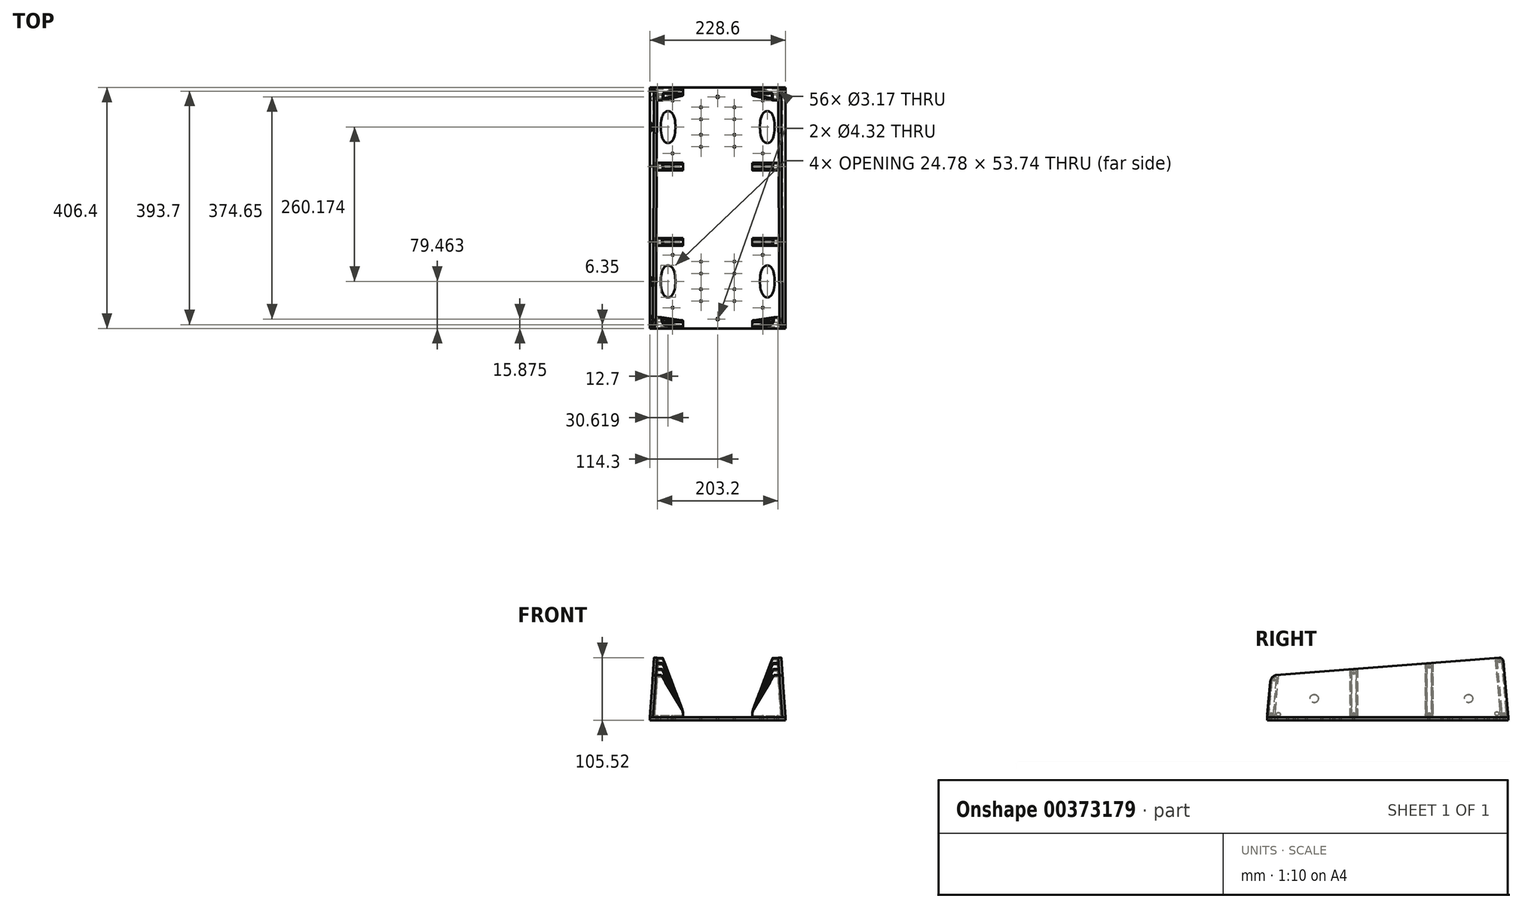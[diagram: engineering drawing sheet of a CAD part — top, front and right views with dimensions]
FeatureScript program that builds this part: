
annotation { "Feature Type Name" : "Feature", "Feature Type Description" : "" }
export const myFeature = defineFeature(function(context is Context, id is Id, definition is map)
    precondition{}
    {
        {
            var Q0;
            Q0=qCreatedBy(makeId("Top.planeOp"),FACE);
            var sketch = newSketch(context, id + "F0", { "sketchPlane" : qUnion([Q0])});
            skLineSegment(sketch, "E0.bottom", {"start": v(-114.3, 203.2) * mm, "end": v(114.3, 203.2) * mm});
            skLineSegment(sketch, "E0.top", {"start": v(-114.3, -203.2) * mm, "end": v(114.3, -203.2) * mm});
            skLineSegment(sketch, "E0.left", {"start": v(-114.3, 203.2) * mm, "end": v(-114.3, -203.2) * mm});
            skLineSegment(sketch, "E0.right", {"start": v(114.3, 203.2) * mm, "end": v(114.3, -203.2) * mm});
            skPoint(sketch, "E0.middle", {"position": v(0, 0) * mm});
            skSolve(sketch);
        }
        {
            var Q0;
            Q0=makeQuery(id+"F0.imprint","IMPRINT",FACE,{"disambiguationData":[TD([[makeQuery(id+"F0.imprint","IMPRINT",EDGE,{"derivedFrom":sQuery(id+"F0.wireOp",EDGE,"E0.bottom")}),-1.0]])]});
            extrude(context, id + "F1", {"entities" : qUnion([Q0]), "depth" : 5.08 * mm});
        }
        {
            var Q0;
            Q0=makeQuery(id+"F1.opExtrude","SWEPT_FACE",FACE,{"disambiguationData":[OSD([sQuery(id+"F0.wireOp",EDGE,"E0.bottom")])]});
            var sketch = newSketch(context, id + "F2", { "sketchPlane" : qUnion([Q0])});
            skLineSegment(sketch, "E1", {"start": v(114.3, 5.08) * mm, "end": v(107.2, 106.68) * mm});
            skLineSegment(sketch, "E2", {"start": v(107.2, 106.68) * mm, "end": v(102.13, 106.33) * mm});
            skLineSegment(sketch, "E3", {"start": v(102.13, 106.33) * mm, "end": v(109.2, 5.08) * mm});
            skLineSegment(sketch, "E4", {"start": v(109.2, 5.08) * mm, "end": v(114.3, 5.08) * mm});
            skSolve(sketch);
        }
        {
            var Q0;
            Q0=makeQuery(id+"F1.opExtrude","SWEPT_FACE",FACE,{"disambiguationData":[OSD([sQuery(id+"F0.wireOp",EDGE,"E0.top")])]});
            var sketch = newSketch(context, id + "F3", { "sketchPlane" : qUnion([Q0])});
            skLineSegment(sketch, "E5", {"start": v(-114.3, 5.08) * mm, "end": v(-109.42, 74.93) * mm});
            skLineSegment(sketch, "E6", {"start": v(-109.42, 74.93) * mm, "end": v(-104.35, 74.58) * mm});
            skLineSegment(sketch, "E7", {"start": v(-104.35, 74.58) * mm, "end": v(-109.2, 5.08) * mm});
            skLineSegment(sketch, "E8", {"start": v(-109.2, 5.08) * mm, "end": v(-114.3, 5.08) * mm});
            skSolve(sketch);
        }
        {
            var Q1;
            Q1=makeQuery(id+"F2.imprint","IMPRINT",FACE,{"disambiguationData":[TD([[makeQuery(id+"F2.imprint","IMPRINT",EDGE,{"derivedFrom":sQuery(id+"F2.wireOp",EDGE,"E1")}),1.0]])]});
            var Q2;
            Q2=makeQuery(id+"F3.imprint","IMPRINT",FACE,{"disambiguationData":[TD([[makeQuery(id+"F3.imprint","IMPRINT",EDGE,{"derivedFrom":sQuery(id+"F3.wireOp",EDGE,"E5")}),-1.0]])]});
            loft(context, id + "F4", {"sheetProfilesArray" : [{ "sheetProfileEntities" : qUnion([Q1]) }, { "sheetProfileEntities" : qUnion([Q2]) }]});
        }
        {
            var Q0;
            Q0=qCreatedBy(makeId("Right.planeOp"),FACE);
            var sketch = newSketch(context, id + "F5", { "sketchPlane" : qUnion([Q0])});
            skLineSegment(sketch, "E9", {"start": v(203.2, 5.08) * mm, "end": v(194.92, 99.72) * mm});
            skLineSegment(sketch, "E10", {"start": v(188.36, 122.29) * mm, "end": v(203.2, 122.29) * mm});
            skLineSegment(sketch, "E11", {"start": v(203.2, 122.29) * mm, "end": v(203.2, 5.08) * mm});
            skLineSegment(sketch, "E12", {"start": v(-203.2, 5.08) * mm, "end": v(-203.2, 91.13) * mm});
            skLineSegment(sketch, "E13", {"start": v(-203.2, 91.13) * mm, "end": v(-192.6, 91.13) * mm});
            skLineSegment(sketch, "E14", {"start": v(-197.97, 64.85) * mm, "end": v(-203.2, 5.08) * mm});
            skArc(sketch, "E15.filletArc", {"start": v(-188.23, 76.1) * mm, "mid": v(-194.92, 72.05) * mm, "end": v(-197.97, 64.85) * mm});
            skLineSegment(sketch, "E16", {"start": v(-192.6, 91.13) * mm, "end": v(-188.23, 76.1) * mm});
            skLineSegment(sketch, "E17", {"start": v(188.1, 105.5) * mm, "end": v(188.1, 105.5) * mm});
            skArc(sketch, "E18.filletArc", {"start": v(194.92, 99.72) * mm, "mid": v(192.7, 104.01) * mm, "end": v(188.1, 105.5) * mm});
            skLineSegment(sketch, "E19", {"start": v(188.1, 105.5) * mm, "end": v(188.36, 122.29) * mm});
            skSolve(sketch);
        }
        {
            var Q0;
            Q0=makeQuery(id+"F5.imprint","IMPRINT",FACE,{"disambiguationData":[TD([[makeQuery(id+"F5.imprint","IMPRINT",EDGE,{"derivedFrom":sQuery(id+"F5.wireOp",EDGE,"E9")}),-1.0]])]});
            var Q1;
            Q1=makeQuery(id+"F5.imprint","IMPRINT",FACE,{"disambiguationData":[TD([[makeQuery(id+"F5.imprint","IMPRINT",EDGE,{"derivedFrom":sQuery(id+"F5.wireOp",EDGE,"E12")}),-1.0]])]});
            extrude(context, id + "F6", {"entities" : qUnion([Q0, Q1]), "operationType" : NewBodyOperationType.REMOVE, "oppositeDirection" : true, "depth" : 203.2 * mm, "hasSecondDirection" : true, "secondDirectionOppositeDirection" : false, "secondDirectionDepth" : 147.32 * mm});
        }
        {
            var Q0;
            Q0=qCreatedBy(makeId("Front.planeOp"),FACE);
            cPlane(context, id + "F7", {"entities" : qUnion([Q0]), "cplaneType" : CPlaneType.OFFSET, "offset" : 127 * mm, "width" : 152.4 * mm, "height" : 152.4 * mm});
        }
        {
            var Q0;
            Q0=makeQuery(id+"F1.opExtrude","CAP_FACE",FACE,{"disambiguationData":[OSD([sQuery(id+"F0.wireOp",EDGE,"E0.bottom"),sQuery(id+"F0.wireOp",EDGE,"E0.top"),sQuery(id+"F0.wireOp",EDGE,"E0.left"),sQuery(id+"F0.wireOp",EDGE,"E0.right")])],"isStart":false});
            var sketch = newSketch(context, id + "F8", { "sketchPlane" : qUnion([Q0])});
            skCircle(sketch, "E20.0", {"center": v(-75.97, -168.27) * mm, "radius": 1.59 * mm});
            skCircle(sketch, "E21.0", {"center": v(-28.17, -157.07) * mm, "radius": 1.59 * mm});
            skCircle(sketch, "E22.0", {"center": v(-28.17, -136.9) * mm, "radius": 1.59 * mm});
            skCircle(sketch, "E23.0", {"center": v(-28.17, -110.58) * mm, "radius": 1.59 * mm});
            skCircle(sketch, "E24.0", {"center": v(-28.17, -90.4) * mm, "radius": 1.59 * mm});
            skCircle(sketch, "E25.0", {"center": v(-75.97, -79.2) * mm, "radius": 1.59 * mm});
            skFitSpline(sketch, "E26.0", {"points": [v(-83.68, -96.87) * mm, v(-83.23, -96.87) * mm, v(-82.57, -96.93) * mm, v(-81.73, -97.12) * mm, v(-80.9, -97.37) * mm, v(-79.92, -97.8) * mm, v(-78.87, -98.46) * mm, v(-77.94, -99.21) * mm, v(-77.13, -100.03) * mm, v(-76.43, -100.88) * mm, v(-75.8, -101.77) * mm, v(-75.26, -102.67) * mm, v(-74.78, -103.59) * mm, v(-74.35, -104.5) * mm, v(-73.85, -105.73) * mm, v(-73.32, -107.27) * mm, v(-72.81, -109.13) * mm, v(-72.4, -110.98) * mm, v(-71.98, -113.43) * mm, v(-71.6, -116.47) * mm, v(-71.37, -120.1) * mm, v(-71.29, -123.74) * mm, v(-71.37, -127.4) * mm, v(-71.61, -131.06) * mm, v(-71.99, -134.1) * mm, v(-72.42, -136.56) * mm, v(-72.83, -138.41) * mm, v(-73.34, -140.26) * mm, v(-73.87, -141.8) * mm, v(-74.38, -143.03) * mm, v(-74.8, -143.95) * mm, v(-75.29, -144.85) * mm, v(-75.83, -145.74) * mm, v(-76.44, -146.61) * mm, v(-77.15, -147.47) * mm, v(-77.96, -148.28) * mm, v(-78.88, -149.02) * mm, v(-79.75, -149.56) * mm, v(-80.5, -149.93) * mm, v(-81.1, -150.16) * mm, v(-81.72, -150.35) * mm, v(-82.57, -150.54) * mm, v(-83.24, -150.6) * mm, v(-83.68, -150.6) * mm]});
            skFitSpline(sketch, "E26.1", {"points": [v(-83.68, -96.87) * mm, v(-84.13, -96.87) * mm, v(-84.79, -96.93) * mm, v(-85.64, -97.12) * mm, v(-86.47, -97.37) * mm, v(-87.45, -97.8) * mm, v(-88.5, -98.46) * mm, v(-89.42, -99.21) * mm, v(-90.23, -100.03) * mm, v(-90.94, -100.88) * mm, v(-91.56, -101.77) * mm, v(-92.1, -102.67) * mm, v(-92.59, -103.59) * mm, v(-93, -104.5) * mm, v(-93.51, -105.73) * mm, v(-94.04, -107.27) * mm, v(-94.55, -109.13) * mm, v(-94.96, -110.98) * mm, v(-95.38, -113.43) * mm, v(-95.75, -116.47) * mm, v(-96, -120.1) * mm, v(-96.07, -123.74) * mm, v(-96, -127.4) * mm, v(-95.75, -131.06) * mm, v(-95.38, -134.1) * mm, v(-94.94, -136.56) * mm, v(-94.53, -138.41) * mm, v(-94.02, -140.26) * mm, v(-93.5, -141.8) * mm, v(-92.99, -143.03) * mm, v(-92.56, -143.95) * mm, v(-92.08, -144.85) * mm, v(-91.53, -145.74) * mm, v(-90.92, -146.61) * mm, v(-90.21, -147.47) * mm, v(-89.4, -148.28) * mm, v(-88.48, -149.02) * mm, v(-87.61, -149.56) * mm, v(-86.85, -149.93) * mm, v(-86.26, -150.16) * mm, v(-85.65, -150.35) * mm, v(-84.79, -150.54) * mm, v(-84.13, -150.6) * mm, v(-83.68, -150.6) * mm]});
            skLineSegment(sketch, "E27", {"start": v(-67.72, -127) * mm, "end": v(-28.17, -127) * mm, "construction": true});
            skLineSegment(sketch, "E28", {"start": v(-88.7, 6.35) * mm, "end": v(82.7, 6.35) * mm, "construction": true});
            skLineSegment(sketch, "E29", {"start": v(0, 92.42) * mm, "end": v(0, -98.09) * mm, "construction": true});
            skCircle(sketch, "E30.MirrorC", {"center": v(28.17, -136.9) * mm, "radius": 1.59 * mm});
            skCircle(sketch, "E31.MirrorC", {"center": v(28.17, -110.58) * mm, "radius": 1.59 * mm});
            skCircle(sketch, "E32.MirrorC", {"center": v(28.17, -157.07) * mm, "radius": 1.59 * mm});
            skCircle(sketch, "E33.MirrorC", {"center": v(75.97, -79.2) * mm, "radius": 1.59 * mm});
            skLineSegment(sketch, "E34.MirrorCS", {"start": v(67.72, -127) * mm, "end": v(28.17, -127) * mm, "construction": true});
            skCircle(sketch, "E35.MirrorC", {"center": v(28.17, -90.4) * mm, "radius": 1.59 * mm});
            skCircle(sketch, "E36.MirrorC", {"center": v(75.97, -168.27) * mm, "radius": 1.59 * mm});
            skFitSpline(sketch, "E37.MirrorCS", {"points": [v(83.68, -96.87) * mm, v(84.13, -96.87) * mm, v(84.79, -96.93) * mm, v(85.64, -97.12) * mm, v(86.47, -97.37) * mm, v(87.45, -97.8) * mm, v(88.5, -98.46) * mm, v(89.42, -99.21) * mm, v(90.23, -100.03) * mm, v(90.94, -100.88) * mm, v(91.56, -101.77) * mm, v(92.1, -102.67) * mm, v(92.59, -103.59) * mm, v(93, -104.5) * mm, v(93.51, -105.73) * mm, v(94.04, -107.27) * mm, v(94.55, -109.13) * mm, v(94.96, -110.98) * mm, v(95.38, -113.43) * mm, v(95.75, -116.47) * mm, v(96, -120.1) * mm, v(96.07, -123.74) * mm, v(96, -127.4) * mm, v(95.75, -131.06) * mm, v(95.38, -134.1) * mm, v(94.94, -136.56) * mm, v(94.53, -138.41) * mm, v(94.02, -140.26) * mm, v(93.5, -141.8) * mm, v(92.99, -143.03) * mm, v(92.56, -143.95) * mm, v(92.08, -144.85) * mm, v(91.53, -145.74) * mm, v(90.92, -146.61) * mm, v(90.21, -147.47) * mm, v(89.4, -148.28) * mm, v(88.48, -149.02) * mm, v(87.61, -149.56) * mm, v(86.85, -149.93) * mm, v(86.26, -150.16) * mm, v(85.65, -150.35) * mm, v(84.79, -150.54) * mm, v(84.13, -150.6) * mm, v(83.68, -150.6) * mm]});
            skFitSpline(sketch, "E38.MirrorCS", {"points": [v(83.68, -96.87) * mm, v(83.23, -96.87) * mm, v(82.57, -96.93) * mm, v(81.73, -97.12) * mm, v(80.9, -97.37) * mm, v(79.92, -97.8) * mm, v(78.87, -98.46) * mm, v(77.94, -99.21) * mm, v(77.13, -100.03) * mm, v(76.43, -100.88) * mm, v(75.8, -101.77) * mm, v(75.26, -102.67) * mm, v(74.78, -103.59) * mm, v(74.35, -104.5) * mm, v(73.85, -105.73) * mm, v(73.32, -107.27) * mm, v(72.81, -109.13) * mm, v(72.4, -110.98) * mm, v(71.98, -113.43) * mm, v(71.6, -116.47) * mm, v(71.37, -120.1) * mm, v(71.29, -123.74) * mm, v(71.37, -127.4) * mm, v(71.61, -131.06) * mm, v(71.99, -134.1) * mm, v(72.42, -136.56) * mm, v(72.83, -138.41) * mm, v(73.34, -140.26) * mm, v(73.87, -141.8) * mm, v(74.38, -143.03) * mm, v(74.8, -143.95) * mm, v(75.29, -144.85) * mm, v(75.83, -145.74) * mm, v(76.44, -146.61) * mm, v(77.15, -147.47) * mm, v(77.96, -148.28) * mm, v(78.88, -149.02) * mm, v(79.75, -149.56) * mm, v(80.5, -149.93) * mm, v(81.1, -150.16) * mm, v(81.72, -150.35) * mm, v(82.57, -150.54) * mm, v(83.24, -150.6) * mm, v(83.68, -150.6) * mm]});
            skCircle(sketch, "E39.MirrorC", {"center": v(28.17, 169.77) * mm, "radius": 1.59 * mm});
            skCircle(sketch, "E40.MirrorC", {"center": v(75.97, 91.9) * mm, "radius": 1.59 * mm});
            skCircle(sketch, "E41.MirrorC", {"center": v(28.17, 149.6) * mm, "radius": 1.59 * mm});
            skCircle(sketch, "E42.MirrorC", {"center": v(28.17, 123.28) * mm, "radius": 1.59 * mm});
            skCircle(sketch, "E43.MirrorC", {"center": v(75.97, 180.97) * mm, "radius": 1.59 * mm});
            skCircle(sketch, "E44.MirrorC", {"center": v(28.17, 103.1) * mm, "radius": 1.59 * mm});
            skLineSegment(sketch, "E45.MirrorCS", {"start": v(67.72, 139.7) * mm, "end": v(28.17, 139.7) * mm, "construction": true});
            skFitSpline(sketch, "E46.MirrorCS", {"points": [v(83.68, 109.57) * mm, v(84.13, 109.57) * mm, v(84.79, 109.63) * mm, v(85.64, 109.82) * mm, v(86.47, 110.07) * mm, v(87.45, 110.5) * mm, v(88.5, 111.16) * mm, v(89.42, 111.91) * mm, v(90.23, 112.73) * mm, v(90.94, 113.58) * mm, v(91.56, 114.47) * mm, v(92.1, 115.37) * mm, v(92.59, 116.29) * mm, v(93, 117.2) * mm, v(93.51, 118.43) * mm, v(94.04, 119.97) * mm, v(94.55, 121.83) * mm, v(94.96, 123.68) * mm, v(95.38, 126.13) * mm, v(95.75, 129.17) * mm, v(96, 132.8) * mm, v(96.07, 136.44) * mm, v(96, 140.1) * mm, v(95.75, 143.76) * mm, v(95.38, 146.8) * mm, v(94.94, 149.26) * mm, v(94.53, 151.11) * mm, v(94.02, 152.96) * mm, v(93.5, 154.5) * mm, v(92.99, 155.73) * mm, v(92.56, 156.65) * mm, v(92.08, 157.55) * mm, v(91.53, 158.44) * mm, v(90.92, 159.31) * mm, v(90.21, 160.17) * mm, v(89.4, 160.98) * mm, v(88.48, 161.72) * mm, v(87.61, 162.26) * mm, v(86.85, 162.63) * mm, v(86.26, 162.86) * mm, v(85.65, 163.05) * mm, v(84.79, 163.24) * mm, v(84.13, 163.3) * mm, v(83.68, 163.3) * mm]});
            skFitSpline(sketch, "E47.MirrorCS", {"points": [v(83.68, 109.57) * mm, v(83.23, 109.57) * mm, v(82.57, 109.63) * mm, v(81.73, 109.82) * mm, v(80.9, 110.07) * mm, v(79.92, 110.5) * mm, v(78.87, 111.16) * mm, v(77.94, 111.91) * mm, v(77.13, 112.73) * mm, v(76.43, 113.58) * mm, v(75.8, 114.47) * mm, v(75.26, 115.37) * mm, v(74.78, 116.29) * mm, v(74.35, 117.2) * mm, v(73.85, 118.43) * mm, v(73.32, 119.97) * mm, v(72.81, 121.83) * mm, v(72.4, 123.68) * mm, v(71.98, 126.13) * mm, v(71.6, 129.17) * mm, v(71.37, 132.8) * mm, v(71.29, 136.44) * mm, v(71.37, 140.1) * mm, v(71.61, 143.76) * mm, v(71.99, 146.8) * mm, v(72.42, 149.26) * mm, v(72.83, 151.11) * mm, v(73.34, 152.96) * mm, v(73.87, 154.5) * mm, v(74.38, 155.73) * mm, v(74.8, 156.65) * mm, v(75.29, 157.55) * mm, v(75.83, 158.44) * mm, v(76.44, 159.31) * mm, v(77.15, 160.17) * mm, v(77.96, 160.98) * mm, v(78.88, 161.72) * mm, v(79.75, 162.26) * mm, v(80.5, 162.63) * mm, v(81.1, 162.86) * mm, v(81.72, 163.05) * mm, v(82.57, 163.24) * mm, v(83.24, 163.3) * mm, v(83.68, 163.3) * mm]});
            skCircle(sketch, "E48.MirrorC", {"center": v(-28.17, 123.28) * mm, "radius": 1.59 * mm});
            skCircle(sketch, "E49.MirrorC", {"center": v(-75.97, 91.9) * mm, "radius": 1.59 * mm});
            skCircle(sketch, "E50.MirrorC", {"center": v(-28.17, 103.1) * mm, "radius": 1.59 * mm});
            skFitSpline(sketch, "E51.MirrorCS", {"points": [v(-83.68, 109.57) * mm, v(-83.23, 109.57) * mm, v(-82.57, 109.63) * mm, v(-81.73, 109.82) * mm, v(-80.9, 110.07) * mm, v(-79.92, 110.5) * mm, v(-78.87, 111.16) * mm, v(-77.94, 111.91) * mm, v(-77.13, 112.73) * mm, v(-76.43, 113.58) * mm, v(-75.8, 114.47) * mm, v(-75.26, 115.37) * mm, v(-74.78, 116.29) * mm, v(-74.35, 117.2) * mm, v(-73.85, 118.43) * mm, v(-73.32, 119.97) * mm, v(-72.81, 121.83) * mm, v(-72.4, 123.68) * mm, v(-71.98, 126.13) * mm, v(-71.6, 129.17) * mm, v(-71.37, 132.8) * mm, v(-71.29, 136.44) * mm, v(-71.37, 140.1) * mm, v(-71.61, 143.76) * mm, v(-71.99, 146.8) * mm, v(-72.42, 149.26) * mm, v(-72.83, 151.11) * mm, v(-73.34, 152.96) * mm, v(-73.87, 154.5) * mm, v(-74.38, 155.73) * mm, v(-74.8, 156.65) * mm, v(-75.29, 157.55) * mm, v(-75.83, 158.44) * mm, v(-76.44, 159.31) * mm, v(-77.15, 160.17) * mm, v(-77.96, 160.98) * mm, v(-78.88, 161.72) * mm, v(-79.75, 162.26) * mm, v(-80.5, 162.63) * mm, v(-81.1, 162.86) * mm, v(-81.72, 163.05) * mm, v(-82.57, 163.24) * mm, v(-83.24, 163.3) * mm, v(-83.68, 163.3) * mm]});
            skLineSegment(sketch, "E52.MirrorCS", {"start": v(-67.72, 139.7) * mm, "end": v(-28.17, 139.7) * mm, "construction": true});
            skCircle(sketch, "E53.MirrorC", {"center": v(-75.97, 180.97) * mm, "radius": 1.59 * mm});
            skCircle(sketch, "E54.MirrorC", {"center": v(-28.17, 169.77) * mm, "radius": 1.59 * mm});
            skCircle(sketch, "E55.MirrorC", {"center": v(-28.17, 149.6) * mm, "radius": 1.59 * mm});
            skFitSpline(sketch, "E56.MirrorCS", {"points": [v(-83.68, 109.57) * mm, v(-84.13, 109.57) * mm, v(-84.79, 109.63) * mm, v(-85.64, 109.82) * mm, v(-86.47, 110.07) * mm, v(-87.45, 110.5) * mm, v(-88.5, 111.16) * mm, v(-89.42, 111.91) * mm, v(-90.23, 112.73) * mm, v(-90.94, 113.58) * mm, v(-91.56, 114.47) * mm, v(-92.1, 115.37) * mm, v(-92.59, 116.29) * mm, v(-93, 117.2) * mm, v(-93.51, 118.43) * mm, v(-94.04, 119.97) * mm, v(-94.55, 121.83) * mm, v(-94.96, 123.68) * mm, v(-95.38, 126.13) * mm, v(-95.75, 129.17) * mm, v(-96, 132.8) * mm, v(-96.07, 136.44) * mm, v(-96, 140.1) * mm, v(-95.75, 143.76) * mm, v(-95.38, 146.8) * mm, v(-94.94, 149.26) * mm, v(-94.53, 151.11) * mm, v(-94.02, 152.96) * mm, v(-93.5, 154.5) * mm, v(-92.99, 155.73) * mm, v(-92.56, 156.65) * mm, v(-92.08, 157.55) * mm, v(-91.53, 158.44) * mm, v(-90.92, 159.31) * mm, v(-90.21, 160.17) * mm, v(-89.4, 160.98) * mm, v(-88.48, 161.72) * mm, v(-87.61, 162.26) * mm, v(-86.85, 162.63) * mm, v(-86.26, 162.86) * mm, v(-85.65, 163.05) * mm, v(-84.79, 163.24) * mm, v(-84.13, 163.3) * mm, v(-83.68, 163.3) * mm]});
            skPoint(sketch, "E57.middle", {"position": v(0, 0) * mm});
            skCircle(sketch, "E58", {"center": v(-101.6, -196.85) * mm, "radius": 1.59 * mm});
            skCircle(sketch, "E59", {"center": v(-76.2, -196.85) * mm, "radius": 1.59 * mm});
            skCircle(sketch, "E60.MirrorC", {"center": v(-76.2, -57.15) * mm, "radius": 1.59 * mm});
            skCircle(sketch, "E61.MirrorC", {"center": v(-101.6, -57.15) * mm, "radius": 1.59 * mm});
            skCircle(sketch, "E62", {"center": v(-101.6, 196.85) * mm, "radius": 1.59 * mm});
            skCircle(sketch, "E63", {"center": v(-76.2, 196.85) * mm, "radius": 1.59 * mm});
            skCircle(sketch, "E64.MirrorC", {"center": v(101.6, 196.85) * mm, "radius": 1.59 * mm});
            skCircle(sketch, "E65.MirrorC", {"center": v(76.2, 196.85) * mm, "radius": 1.59 * mm});
            skCircle(sketch, "E66.MirrorC", {"center": v(101.6, -57.15) * mm, "radius": 1.59 * mm});
            skCircle(sketch, "E67.MirrorC", {"center": v(76.2, -57.15) * mm, "radius": 1.59 * mm});
            skCircle(sketch, "E68.MirrorC", {"center": v(101.6, -196.85) * mm, "radius": 1.59 * mm});
            skCircle(sketch, "E69.MirrorC", {"center": v(76.2, -196.85) * mm, "radius": 1.59 * mm});
            skCircle(sketch, "E70", {"center": v(-101.6, 69.85) * mm, "radius": 1.59 * mm});
            skCircle(sketch, "E71", {"center": v(-76.2, 69.85) * mm, "radius": 1.59 * mm});
            skCircle(sketch, "E72.MirrorC", {"center": v(76.2, 69.85) * mm, "radius": 1.59 * mm});
            skCircle(sketch, "E73.MirrorC", {"center": v(101.6, 69.85) * mm, "radius": 1.59 * mm});
            skPoint(sketch, "E57.right.start.orphan", {"position": v(114.3, 203.2) * mm});
            skPoint(sketch, "E57.left.start.orphan", {"position": v(-114.3, 203.2) * mm});
            skPoint(sketch, "E57.top.end.orphan", {"position": v(114.3, -203.2) * mm});
            skPoint(sketch, "E57.top.start.orphan", {"position": v(-114.3, -203.2) * mm});
            skCircle(sketch, "E74", {"center": v(0, 187.33) * mm, "radius": 2.16 * mm});
            skCircle(sketch, "E75", {"center": v(0, -187.32) * mm, "radius": 2.16 * mm});
            skSolve(sketch);
        }
        {
            var Q0;
            Q0=makeQuery(id+"F4.opLoft","SWEPT_FACE",FACE,{"disambiguationData":[OSD([sQuery(id+"F0.wireOp",EDGE,"E0.bottom"),sQuery(id+"F0.wireOp",EDGE,"E0.top"),sQuery(id+"F0.wireOp",EDGE,"E0.left"),sQuery(id+"F2.wireOp",EDGE,"E1"),sQuery(id+"F2.wireOp",EDGE,"E2"),sQuery(id+"F2.wireOp",EDGE,"E4"),sQuery(id+"F3.wireOp",EDGE,"E5"),sQuery(id+"F3.wireOp",EDGE,"E6"),sQuery(id+"F3.wireOp",EDGE,"E8")])]});
            var sketch = newSketch(context, id + "F9", { "sketchPlane" : qUnion([Q0])});
            skLineSegment(sketch, "E76", {"start": v(197.97, 57) * mm, "end": v(197.97, 57) * mm});
            skLineSegment(sketch, "E77", {"start": v(196.83, -2.9) * mm, "end": v(190.63, 68.1) * mm, "construction": true});
            skLineSegment(sketch, "E78", {"start": v(-196.83, -2.9) * mm, "end": v(-188.04, 97.76) * mm, "construction": true});
            skLineSegment(sketch, "E79", {"start": v(-69.85, -2.9) * mm, "end": v(-69.85, 88.5) * mm, "construction": true});
            skLineSegment(sketch, "E80", {"start": v(57.15, -2.9) * mm, "end": v(57.15, 78.55) * mm, "construction": true});
            skCircle(sketch, "E81", {"center": v(-196.27, 3.42) * mm, "radius": 1.59 * mm});
            skCircle(sketch, "E82", {"center": v(-188.6, 91.43) * mm, "radius": 1.59 * mm});
            skCircle(sketch, "E83", {"center": v(-69.85, 82.15) * mm, "radius": 1.59 * mm});
            skCircle(sketch, "E84", {"center": v(-69.85, 3.44) * mm, "radius": 1.59 * mm});
            skCircle(sketch, "E85", {"center": v(57.15, 72.2) * mm, "radius": 1.59 * mm});
            skCircle(sketch, "E86", {"center": v(57.15, 3.44) * mm, "radius": 1.59 * mm});
            skCircle(sketch, "E87", {"center": v(196.27, 3.42) * mm, "radius": 1.59 * mm});
            skCircle(sketch, "E88", {"center": v(191.3, 60.5) * mm, "radius": 1.59 * mm});
            skCircle(sketch, "E89", {"center": v(184.15, 2.17) * mm, "radius": 3.24 * mm});
            skCircle(sketch, "E90", {"center": v(-184.15, 3.44) * mm, "radius": 3.24 * mm});
            skCircle(sketch, "E91", {"center": v(123.74, 28.84) * mm, "radius": 6.99 * mm});
            skCircle(sketch, "E92", {"center": v(-136.44, 28.84) * mm, "radius": 6.99 * mm});
            skSolve(sketch);
        }
        {
            var Q0;
            Q0=makeQuery(id+"F4.opLoft","SWEPT_BODY",BODY,{"disambiguationData":[OSD([makeQuery(id+"F2.imprint","IMPRINT",FACE,{"disambiguationData":[TD([[makeQuery(id+"F2.imprint","IMPRINT",EDGE,{"derivedFrom":sQuery(id+"F2.wireOp",EDGE,"E1")}),1.0]])]}),makeQuery(id+"F3.imprint","IMPRINT",FACE,{"disambiguationData":[TD([[makeQuery(id+"F3.imprint","IMPRINT",EDGE,{"derivedFrom":sQuery(id+"F3.wireOp",EDGE,"E5")}),-1.0]])]})])]});
            var Q1;
            Q1=qCreatedBy(makeId("Right.planeOp"),FACE);
            mirror(context, id + "F10", {"entities" : qUnion([Q0]), "mirrorPlane" : qUnion([Q1])});
        }
        {
            var Q0;
            Q0=makeQuery(id+"F6.boolean.opBoolean","COPY",FACE,{"derivedFrom":makeQuery(id+"F6.opExtrude","SWEPT_FACE",FACE,{"disambiguationData":[OSD([sQuery(id+"F5.wireOp",EDGE,"E14")])]})});
            cPlane(context, id + "F11", {"entities" : qUnion([Q0]), "cplaneType" : CPlaneType.OFFSET, "offset" : 0 * mm, "width" : 152.4 * mm, "height" : 152.4 * mm});
        }
        {
            var Q0;
            Q0=qCreatedBy(id+"F11.planeOp",FACE);
            var sketch = newSketch(context, id + "F12", { "sketchPlane" : qUnion([Q0])});
            skLineSegment(sketch, "E93", {"start": v(-58.4, -12.65) * mm, "end": v(-109.2, -12.65) * mm});
            skLineSegment(sketch, "E94", {"start": v(-109.2, -12.65) * mm, "end": v(-104.31, 57.6) * mm});
            skLineSegment(sketch, "E95", {"start": v(-104.31, 57.6) * mm, "end": v(-94.79, 57.6) * mm});
            skLineSegment(sketch, "E96", {"start": v(-94.79, 57.6) * mm, "end": v(-58.4, -3.12) * mm});
            skLineSegment(sketch, "E97", {"start": v(-58.4, -3.12) * mm, "end": v(-58.4, -12.65) * mm});
            skSolve(sketch);
        }
        {
            var Q0;
            Q0=qCreatedBy(id+"F11.planeOp",FACE);
            cPlane(context, id + "F13", {"entities" : qUnion([Q0]), "cplaneType" : CPlaneType.OFFSET, "offset" : 12.7 * mm, "oppositeDirection" : true, "width" : 152.4 * mm, "height" : 152.4 * mm});
        }
        {
            var Q0;
            Q0=qCreatedBy(id+"F13.planeOp",FACE);
            var sketch = newSketch(context, id + "F14", { "sketchPlane" : qUnion([Q0])});
            skLineSegment(sketch, "E98", {"start": v(-94.72, 59.7) * mm, "end": v(-58.4, -2.01) * mm});
            skLineSegment(sketch, "E99", {"start": v(-58.4, -2.01) * mm, "end": v(-58.4, -11.54) * mm});
            skLineSegment(sketch, "E100", {"start": v(-58.4, -11.54) * mm, "end": v(-109.2, -11.54) * mm});
            skLineSegment(sketch, "E101", {"start": v(-104.24, 59.7) * mm, "end": v(-94.72, 59.7) * mm});
            skLineSegment(sketch, "E102", {"start": v(-104.24, 59.7) * mm, "end": v(-109.2, -11.54) * mm});
            skSolve(sketch);
        }
        {
            var Q1;
            Q1=makeQuery(id+"F12.imprint","IMPRINT",FACE,{"disambiguationData":[TD([[makeQuery(id+"F12.imprint","IMPRINT",EDGE,{"derivedFrom":sQuery(id+"F12.wireOp",EDGE,"E93")}),-1.0]])]});
            var Q2;
            Q2=makeQuery(id+"F14.imprint","IMPRINT",FACE,{"disambiguationData":[TD([[makeQuery(id+"F14.imprint","IMPRINT",EDGE,{"derivedFrom":sQuery(id+"F14.wireOp",EDGE,"E98")}),-1.0]])]});
            loft(context, id + "F15", {"sheetProfilesArray" : [{ "sheetProfileEntities" : qUnion([Q1]) }, { "sheetProfileEntities" : qUnion([Q2]) }]});
        }
        {
            var Q0;
            Q0=makeQuery(id+"F15.opLoft","MID_CAP_EDGE",EDGE,{"disambiguationData":[OSD([sQuery(id+"F12.wireOp",EDGE,"E94"),sQuery(id+"F12.wireOp",EDGE,"E95"),sQuery(id+"F12.wireOp",EDGE,"E96")])],"capPos":0.0});
            fillet(context, id + "F16", {"entities" : qUnion([Q0]), "radius" : 12.7 * mm, "tangentPropagation" : true, "allowEdgeOverflow" : false});
        }
        {
            var Q0;
            Q0=makeQuery(id+"F15.opLoft","SWEPT_FACE",FACE,{"disambiguationData":[OSD([sQuery(id+"F12.wireOp",EDGE,"E95"),sQuery(id+"F12.wireOp",EDGE,"E96"),sQuery(id+"F12.wireOp",EDGE,"E97"),sQuery(id+"F14.wireOp",EDGE,"E98"),sQuery(id+"F14.wireOp",EDGE,"E99"),sQuery(id+"F14.wireOp",EDGE,"E101")])]});
            var Q1;
            Q1=makeQuery(id+"F15.opLoft","SWEPT_FACE",FACE,{"disambiguationData":[OSD([sQuery(id+"F12.wireOp",EDGE,"E93"),sQuery(id+"F12.wireOp",EDGE,"E96"),sQuery(id+"F12.wireOp",EDGE,"E97"),sQuery(id+"F14.wireOp",EDGE,"E98"),sQuery(id+"F14.wireOp",EDGE,"E99"),sQuery(id+"F14.wireOp",EDGE,"E100")])]});
            shell(context, id + "F17", {"entities" : qUnion([Q0, Q1]), "thickness" : 2.54 * mm});
        }
        {
            var Q0;
            Q0=sQuery(id+"F9.wireOp",EDGE,"E80");
            cPlane(context, id + "F18", {"entities" : qUnion([Q0]), "cplaneType" : CPlaneType.LINE_ANGLE, "offset" : 25.4 * mm, "angle" : 90 * degree, "width" : 152.4 * mm, "height" : 152.4 * mm});
        }
        {
            var Q0;
            Q0=qCreatedBy(id+"F18.planeOp",FACE);
            var sketch = newSketch(context, id + "F19", { "sketchPlane" : qUnion([Q0])});
            skLineSegment(sketch, "E103", {"start": v(103.5, 86.67) * mm, "end": v(93.98, 86.67) * mm});
            skLineSegment(sketch, "E104", {"start": v(93.98, 86.67) * mm, "end": v(58.4, 14.6) * mm});
            skLineSegment(sketch, "E105", {"start": v(58.4, 14.6) * mm, "end": v(58.4, 5.08) * mm});
            skLineSegment(sketch, "E106", {"start": v(58.4, 5.08) * mm, "end": v(109.2, 5.08) * mm});
            skLineSegment(sketch, "E107", {"start": v(109.2, 5.08) * mm, "end": v(103.5, 86.67) * mm});
            skSolve(sketch);
        }
        {
            var Q0;
            Q0=makeQuery(id+"F19.imprint","IMPRINT",FACE,{"disambiguationData":[TD([[makeQuery(id+"F19.imprint","IMPRINT",EDGE,{"derivedFrom":sQuery(id+"F19.wireOp",EDGE,"E103")}),1.0]])]});
            extrude(context, id + "F20", {"entities" : qUnion([Q0]), "depth" : 6.35 * mm, "hasSecondDirection" : true, "secondDirectionOppositeDirection" : true, "secondDirectionDepth" : 6.35 * mm});
        }
        {
            var Q0;
            Q0=qCreatedBy(makeId("Right.planeOp"),FACE);
            var sketch = newSketch(context, id + "F21", { "sketchPlane" : qUnion([Q0])});
            skLineSegment(sketch, "E108", {"start": v(-63.83, 85.46) * mm, "end": v(-49.7, 86.57) * mm});
            skLineSegment(sketch, "E109", {"start": v(-49.7, 86.57) * mm, "end": v(-49.7, 86.98) * mm});
            skLineSegment(sketch, "E110", {"start": v(-49.7, 86.98) * mm, "end": v(-63.84, 87.2) * mm});
            skLineSegment(sketch, "E111", {"start": v(-63.84, 87.2) * mm, "end": v(-63.83, 85.46) * mm});
            skSolve(sketch);
        }
        {
            var Q0;
            Q0=makeQuery(id+"F21.imprint","IMPRINT",FACE,{"disambiguationData":[TD([[makeQuery(id+"F21.imprint","IMPRINT",EDGE,{"derivedFrom":sQuery(id+"F21.wireOp",EDGE,"E108")}),1.0]])]});
            var Q1;
            Q1=makeQuery(id+"F20.opExtrude","SWEPT_FACE",FACE,{"disambiguationData":[OSD([sQuery(id+"F19.wireOp",EDGE,"E107")])]});
            extrude(context, id + "F22", {"entities" : qUnion([Q0]), "operationType" : NewBodyOperationType.REMOVE, "endBound" : BoundingType.UP_TO_SURFACE, "oppositeDirection" : true, "endBoundEntityFace" : qUnion([Q1]), "depth" : 25.4 * mm});
        }
        {
            var Q0;
            Q0=makeQuery(id+"F20.opExtrude","SWEPT_FACE",FACE,{"disambiguationData":[OSD([sQuery(id+"F19.wireOp",EDGE,"E104")])]});
            var Q1;
            Q1=makeQuery(id+"F20.opExtrude","SWEPT_FACE",FACE,{"disambiguationData":[OSD([sQuery(id+"F19.wireOp",EDGE,"E105")])]});
            shell(context, id + "F23", {"entities" : qUnion([Q0, Q1]), "thickness" : 2.54 * mm});
        }
        {
            var Q0;
            Q0=sQuery(id+"F9.wireOp",EDGE,"E79");
            cPlane(context, id + "F24", {"entities" : qUnion([Q0]), "cplaneType" : CPlaneType.LINE_ANGLE, "offset" : 25.4 * mm, "angle" : 90 * degree, "width" : 152.4 * mm, "height" : 152.4 * mm});
        }
        {
            var Q0;
            Q0=qCreatedBy(id+"F24.planeOp",FACE);
            var sketch = newSketch(context, id + "F25", { "sketchPlane" : qUnion([Q0])});
            skLineSegment(sketch, "E112", {"start": v(102.8, 96.7) * mm, "end": v(109.2, 5.08) * mm});
            skLineSegment(sketch, "E113", {"start": v(109.2, 5.08) * mm, "end": v(58.4, 5.08) * mm});
            skLineSegment(sketch, "E114", {"start": v(58.4, 5.08) * mm, "end": v(58.4, 14.6) * mm});
            skLineSegment(sketch, "E115", {"start": v(58.4, 14.6) * mm, "end": v(93.28, 96.7) * mm});
            skLineSegment(sketch, "E116", {"start": v(93.28, 96.7) * mm, "end": v(102.8, 96.7) * mm});
            skSolve(sketch);
        }
        {
            var Q0;
            Q0=makeQuery(id+"F25.imprint","IMPRINT",FACE,{"disambiguationData":[TD([[makeQuery(id+"F25.imprint","IMPRINT",EDGE,{"derivedFrom":sQuery(id+"F25.wireOp",EDGE,"E112")}),-1.0]])]});
            extrude(context, id + "F26", {"entities" : qUnion([Q0]), "depth" : 6.35 * mm, "hasSecondDirection" : true, "secondDirectionOppositeDirection" : true, "secondDirectionDepth" : 6.35 * mm});
        }
        {
            var Q0;
            Q0=qCreatedBy(makeId("Right.planeOp"),FACE);
            var sketch = newSketch(context, id + "F27", { "sketchPlane" : qUnion([Q0])});
            skLineSegment(sketch, "E117", {"start": v(79.55, 96.67) * mm, "end": v(60.68, 95.2) * mm});
            skLineSegment(sketch, "E118", {"start": v(60.68, 95.2) * mm, "end": v(60.68, 98.07) * mm});
            skLineSegment(sketch, "E119", {"start": v(60.68, 98.07) * mm, "end": v(79.55, 98.07) * mm});
            skLineSegment(sketch, "E120", {"start": v(79.55, 98.07) * mm, "end": v(79.55, 96.67) * mm});
            skSolve(sketch);
        }
        {
            var Q0;
            Q0=makeQuery(id+"F27.imprint","IMPRINT",FACE,{"disambiguationData":[TD([[makeQuery(id+"F27.imprint","IMPRINT",EDGE,{"derivedFrom":sQuery(id+"F27.wireOp",EDGE,"E117")}),-1.0]])]});
            var Q1;
            Q1=makeQuery(id+"F26.opExtrude","SWEPT_FACE",FACE,{"disambiguationData":[OSD([sQuery(id+"F25.wireOp",EDGE,"E112")])]});
            extrude(context, id + "F28", {"entities" : qUnion([Q0]), "operationType" : NewBodyOperationType.REMOVE, "endBound" : BoundingType.UP_TO_SURFACE, "oppositeDirection" : true, "endBoundEntityFace" : qUnion([Q1]), "depth" : 25.4 * mm});
        }
        {
            var Q0;
            Q0=makeQuery(id+"F26.opExtrude","SWEPT_FACE",FACE,{"disambiguationData":[OSD([sQuery(id+"F25.wireOp",EDGE,"E115")])]});
            var Q1;
            Q1=makeQuery(id+"F26.opExtrude","SWEPT_FACE",FACE,{"disambiguationData":[OSD([sQuery(id+"F25.wireOp",EDGE,"E114")])]});
            shell(context, id + "F29", {"entities" : qUnion([Q0, Q1]), "thickness" : 2.54 * mm});
        }
        {
            var Q0;
            Q0=makeQuery(id+"F6.boolean.opBoolean","COPY",FACE,{"derivedFrom":makeQuery(id+"F6.opExtrude","SWEPT_FACE",FACE,{"disambiguationData":[OSD([sQuery(id+"F5.wireOp",EDGE,"E9")])]})});
            cPlane(context, id + "F30", {"entities" : qUnion([Q0]), "cplaneType" : CPlaneType.OFFSET, "offset" : 0 * mm, "width" : 152.4 * mm, "height" : 152.4 * mm});
        }
        {
            var Q0;
            Q0=qCreatedBy(id+"F30.planeOp",FACE);
            cPlane(context, id + "F31", {"entities" : qUnion([Q0]), "cplaneType" : CPlaneType.OFFSET, "offset" : 12.7 * mm, "oppositeDirection" : true, "width" : 152.4 * mm, "height" : 152.4 * mm});
        }
        {
            var Q0;
            Q0=qCreatedBy(id+"F30.planeOp",FACE);
            var sketch = newSketch(context, id + "F32", { "sketchPlane" : qUnion([Q0])});
            skLineSegment(sketch, "E121", {"start": v(109.2, -12.65) * mm, "end": v(58.4, -12.65) * mm});
            skLineSegment(sketch, "E122", {"start": v(58.4, -12.65) * mm, "end": v(58.4, -3.12) * mm});
            skLineSegment(sketch, "E123", {"start": v(58.4, -3.12) * mm, "end": v(92.67, 87.96) * mm});
            skLineSegment(sketch, "E124", {"start": v(92.67, 87.96) * mm, "end": v(102.2, 87.96) * mm});
            skLineSegment(sketch, "E125", {"start": v(102.2, 87.96) * mm, "end": v(109.2, -12.65) * mm});
            skSolve(sketch);
        }
        {
            var Q0;
            Q0=qCreatedBy(id+"F31.planeOp",FACE);
            var sketch = newSketch(context, id + "F33", { "sketchPlane" : qUnion([Q0])});
            skLineSegment(sketch, "E126", {"start": v(102.25, 88.41) * mm, "end": v(109.2, -11.54) * mm});
            skLineSegment(sketch, "E127", {"start": v(109.2, -11.54) * mm, "end": v(58.4, -11.54) * mm});
            skLineSegment(sketch, "E128", {"start": v(58.4, -11.54) * mm, "end": v(58.4, -2.01) * mm});
            skLineSegment(sketch, "E129", {"start": v(58.4, -2.01) * mm, "end": v(92.72, 88.41) * mm});
            skLineSegment(sketch, "E130", {"start": v(92.72, 88.41) * mm, "end": v(102.25, 88.41) * mm});
            skSolve(sketch);
        }
        {
            var Q0;
            Q0=makeQuery(id+"F32.imprint","IMPRINT",FACE,{"disambiguationData":[TD([[makeQuery(id+"F32.imprint","IMPRINT",EDGE,{"derivedFrom":sQuery(id+"F32.wireOp",EDGE,"E121")}),-1.0]])]});
            var Q1;
            Q1=makeQuery(id+"F33.imprint","IMPRINT",FACE,{"disambiguationData":[TD([[makeQuery(id+"F33.imprint","IMPRINT",EDGE,{"derivedFrom":sQuery(id+"F33.wireOp",EDGE,"E126")}),-1.0]])]});
            loft(context, id + "F34", {"sheetProfilesArray" : [{ "sheetProfileEntities" : qUnion([Q0]) }, { "sheetProfileEntities" : qUnion([Q1]) }]});
        }
        {
            var Q0;
            Q0=makeQuery(id+"F34.opLoft","MID_CAP_EDGE",EDGE,{"disambiguationData":[OSD([sQuery(id+"F32.wireOp",EDGE,"E123"),sQuery(id+"F32.wireOp",EDGE,"E124"),sQuery(id+"F32.wireOp",EDGE,"E125")])],"capPos":0.0});
            fillet(context, id + "F35", {"entities" : qUnion([Q0]), "radius" : 6.35 * mm, "tangentPropagation" : true, "allowEdgeOverflow" : false});
        }
        {
            var Q0;
            Q0=makeQuery(id+"F34.opLoft","SWEPT_FACE",FACE,{"disambiguationData":[OSD([sQuery(id+"F32.wireOp",EDGE,"E122"),sQuery(id+"F32.wireOp",EDGE,"E123"),sQuery(id+"F32.wireOp",EDGE,"E124"),sQuery(id+"F33.wireOp",EDGE,"E128"),sQuery(id+"F33.wireOp",EDGE,"E129"),sQuery(id+"F33.wireOp",EDGE,"E130")])]});
            var Q1;
            Q1=makeQuery(id+"F34.opLoft","SWEPT_FACE",FACE,{"disambiguationData":[OSD([sQuery(id+"F32.wireOp",EDGE,"E121"),sQuery(id+"F32.wireOp",EDGE,"E122"),sQuery(id+"F32.wireOp",EDGE,"E123"),sQuery(id+"F33.wireOp",EDGE,"E127"),sQuery(id+"F33.wireOp",EDGE,"E128"),sQuery(id+"F33.wireOp",EDGE,"E129")])]});
            shell(context, id + "F36", {"entities" : qUnion([Q0, Q1]), "thickness" : 2.54 * mm});
        }
        {
            var Q0;
            Q0=makeQuery(id+"F15.opLoft","SWEPT_EDGE",EDGE,{"disambiguationData":[OSD([sQuery(id+"F12.wireOp",EDGE,"E96"),sQuery(id+"F12.wireOp",EDGE,"E97"),sQuery(id+"F14.wireOp",EDGE,"E98"),sQuery(id+"F14.wireOp",EDGE,"E99")])]});
            var Q1;
            Q1=makeQuery(id+"F17.opShell","OFFSET_EDGE",EDGE,{"disambiguationData":[OSD([sQuery(id+"F12.wireOp",EDGE,"E96"),sQuery(id+"F12.wireOp",EDGE,"E97"),sQuery(id+"F14.wireOp",EDGE,"E98"),sQuery(id+"F14.wireOp",EDGE,"E99")])]});
            var Q2;
            Q2=makeQuery(id+"F23.opShell","OFFSET_EDGE",EDGE,{"disambiguationData":[OSD([sQuery(id+"F19.wireOp",EDGE,"E104"),sQuery(id+"F19.wireOp",EDGE,"E105")])]});
            var Q3;
            Q3=makeQuery(id+"F20.opExtrude","SWEPT_EDGE",EDGE,{"disambiguationData":[OSD([sQuery(id+"F19.wireOp",EDGE,"E104"),sQuery(id+"F19.wireOp",EDGE,"E105")])]});
            var Q4;
            Q4=makeQuery(id+"F29.opShell","OFFSET_EDGE",EDGE,{"disambiguationData":[OSD([sQuery(id+"F25.wireOp",EDGE,"E114"),sQuery(id+"F25.wireOp",EDGE,"E115")])]});
            var Q5;
            Q5=makeQuery(id+"F26.opExtrude","SWEPT_EDGE",EDGE,{"disambiguationData":[OSD([sQuery(id+"F25.wireOp",EDGE,"E114"),sQuery(id+"F25.wireOp",EDGE,"E115")])]});
            var Q6;
            Q6=makeQuery(id+"F36.opShell","OFFSET_EDGE",EDGE,{"disambiguationData":[OSD([sQuery(id+"F32.wireOp",EDGE,"E122"),sQuery(id+"F32.wireOp",EDGE,"E123"),sQuery(id+"F33.wireOp",EDGE,"E128"),sQuery(id+"F33.wireOp",EDGE,"E129")])]});
            var Q7;
            Q7=makeQuery(id+"F34.opLoft","SWEPT_EDGE",EDGE,{"disambiguationData":[OSD([sQuery(id+"F32.wireOp",EDGE,"E122"),sQuery(id+"F32.wireOp",EDGE,"E123"),sQuery(id+"F33.wireOp",EDGE,"E128"),sQuery(id+"F33.wireOp",EDGE,"E129")])]});
            fillet(context, id + "F37", {"entities" : qUnion([Q0, Q1, Q2, Q3, Q4, Q5, Q6, Q7]), "radius" : 19.05 * mm, "tangentPropagation" : true, "allowEdgeOverflow" : false});
        }
        {
            var Q0;
            Q0=qSketchRegion(id+"F9",true);
            var Q1;
            Q1=makeQuery(id+"F17.opShell","OFFSET_FACE",FACE,{"disambiguationData":[OSD([sQuery(id+"F12.wireOp",EDGE,"E93"),sQuery(id+"F12.wireOp",EDGE,"E94"),sQuery(id+"F12.wireOp",EDGE,"E95"),sQuery(id+"F14.wireOp",EDGE,"E100"),sQuery(id+"F14.wireOp",EDGE,"E101"),sQuery(id+"F14.wireOp",EDGE,"E102")])]});
            extrude(context, id + "F38", {"entities" : qUnion([Q0]), "operationType" : NewBodyOperationType.REMOVE, "oppositeDirection" : true, "endBoundEntityFace" : qUnion([Q1]), "depth" : 10.16 * mm});
        }
        {
            var Q0;
            Q0=makeQuery(id+"F15.opLoft","SWEPT_BODY",BODY,{"disambiguationData":[OSD([makeQuery(id+"F12.imprint","IMPRINT",FACE,{"disambiguationData":[TD([[makeQuery(id+"F12.imprint","IMPRINT",EDGE,{"derivedFrom":sQuery(id+"F12.wireOp",EDGE,"E93")}),-1.0]])]}),makeQuery(id+"F14.imprint","IMPRINT",FACE,{"disambiguationData":[TD([[makeQuery(id+"F14.imprint","IMPRINT",EDGE,{"derivedFrom":sQuery(id+"F14.wireOp",EDGE,"E98")}),-1.0]])]})])]});
            var Q1;
            Q1=makeQuery(id+"F20.opExtrude","SWEPT_BODY",BODY,{"disambiguationData":[OSD([sQuery(id+"F19.wireOp",EDGE,"E103"),sQuery(id+"F19.wireOp",EDGE,"E104"),sQuery(id+"F19.wireOp",EDGE,"E105"),sQuery(id+"F19.wireOp",EDGE,"E106"),sQuery(id+"F19.wireOp",EDGE,"E107")])]});
            var Q2;
            Q2=makeQuery(id+"F26.opExtrude","SWEPT_BODY",BODY,{"disambiguationData":[OSD([sQuery(id+"F25.wireOp",EDGE,"E112"),sQuery(id+"F25.wireOp",EDGE,"E113"),sQuery(id+"F25.wireOp",EDGE,"E114"),sQuery(id+"F25.wireOp",EDGE,"E115"),sQuery(id+"F25.wireOp",EDGE,"E116")])]});
            var Q3;
            Q3=makeQuery(id+"F34.opLoft","SWEPT_BODY",BODY,{"disambiguationData":[OSD([makeQuery(id+"F32.imprint","IMPRINT",FACE,{"disambiguationData":[TD([[makeQuery(id+"F32.imprint","IMPRINT",EDGE,{"derivedFrom":sQuery(id+"F32.wireOp",EDGE,"E121")}),-1.0]])]}),makeQuery(id+"F33.imprint","IMPRINT",FACE,{"disambiguationData":[TD([[makeQuery(id+"F33.imprint","IMPRINT",EDGE,{"derivedFrom":sQuery(id+"F33.wireOp",EDGE,"E126")}),-1.0]])]})])]});
            var Q4;
            Q4=qCreatedBy(makeId("Right.planeOp"),FACE);
            mirror(context, id + "F39", {"entities" : qUnion([Q0, Q1, Q2, Q3]), "mirrorPlane" : qUnion([Q4])});
        }
        {
            var Q0;
            Q0=qSketchRegion(id+"F8",true);
            extrude(context, id + "F40", {"entities" : qUnion([Q0]), "operationType" : NewBodyOperationType.REMOVE, "oppositeDirection" : true, "depth" : 25.4 * mm, "hasSecondDirection" : true, "secondDirectionOppositeDirection" : false, "secondDirectionDepth" : 12.7 * mm});
        }
    });
